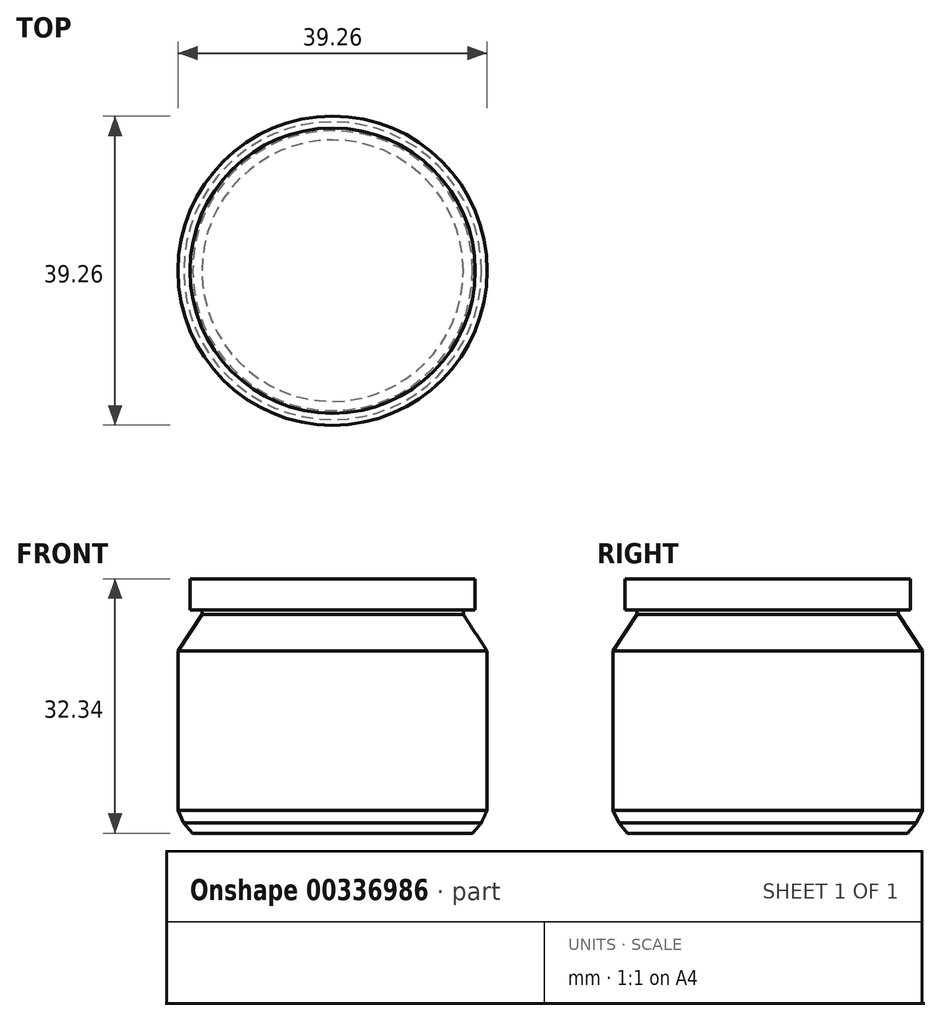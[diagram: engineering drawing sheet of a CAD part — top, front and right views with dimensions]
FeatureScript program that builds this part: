
annotation { "Feature Type Name" : "Feature", "Feature Type Description" : "" }
export const myFeature = defineFeature(function(context is Context, id is Id, definition is map)
    precondition{}
    {
        {
            var Q0;
            Q0=qCreatedBy(makeId("Front.planeOp"),FACE);
            var sketch = newSketch(context, id + "F0", { "sketchPlane" : qUnion([Q0])});
            skLineSegment(sketch, "E0", {"start": v(0, 0) * mm, "end": v(0, 32.34) * mm, "construction": true});
            skLineSegment(sketch, "E1", {"start": v(0, 0) * mm, "end": v(-17.78, 0) * mm, "construction": true});
            skLineSegment(sketch, "E2", {"start": v(-17.78, 0) * mm, "end": v(-18.9, 1.34) * mm});
            skLineSegment(sketch, "E3", {"start": v(-18.9, 1.34) * mm, "end": v(-19.63, 2.93) * mm});
            skLineSegment(sketch, "E4", {"start": v(-19.63, 2.93) * mm, "end": v(-19.63, 23.17) * mm});
            skLineSegment(sketch, "E5", {"start": v(-19.63, 23.17) * mm, "end": v(-16.6, 27.79) * mm});
            skLineSegment(sketch, "E6", {"start": v(-16.6, 27.79) * mm, "end": v(-16.6, 28.38) * mm});
            skPoint(sketch, "E7.end.orphan", {"position": v(-17.26, 31.68) * mm});
            skPoint(sketch, "E8.end.orphan", {"position": v(-17.78, 30.75) * mm});
            skPoint(sketch, "E8.start.orphan", {"position": v(-17.26, 30.75) * mm});
            skLineSegment(sketch, "E9", {"start": v(-16.6, 28.38) * mm, "end": v(-18.12, 28.38) * mm});
            skLineSegment(sketch, "E10", {"start": v(-18.12, 28.38) * mm, "end": v(-18.12, 32.34) * mm});
            skLineSegment(sketch, "E11", {"start": v(-18.12, 32.34) * mm, "end": v(0, 32.34) * mm});
            skLineSegment(sketch, "E12", {"start": v(-16.6, 28.38) * mm, "end": v(0, 28.38) * mm});
            skLineSegment(sketch, "E13", {"start": v(0, 32.34) * mm, "end": v(0, 0) * mm});
            skLineSegment(sketch, "E14", {"start": v(0, 0) * mm, "end": v(-17.78, 0) * mm});
            skSolve(sketch);
        }
        {
            var Q0;
            Q0=makeQuery(id+"F0.imprint","IMPRINT",FACE,{"disambiguationData":[TD([[makeQuery(id+"F0.imprint","IMPRINT",EDGE,{"derivedFrom":sQuery(id+"F0.wireOp",EDGE,"E9")}),-1.0]])]});
            var Q1;
            Q1=makeQuery(id+"F0.imprint","IMPRINT",FACE,{"disambiguationData":[TD([[makeQuery(id+"F0.imprint","IMPRINT",EDGE,{"derivedFrom":sQuery(id+"F0.wireOp",EDGE,"E2")}),-1.0]])]});
            var Q2;
            Q2=sQuery(id+"F0.wireOp",EDGE,"E13");
            revolve(context, id + "F1", {"entities" : qUnion([Q0, Q1]), "axis" : qUnion([Q2]), "revolveType" : RevolveType.FULL});
        }
    });
